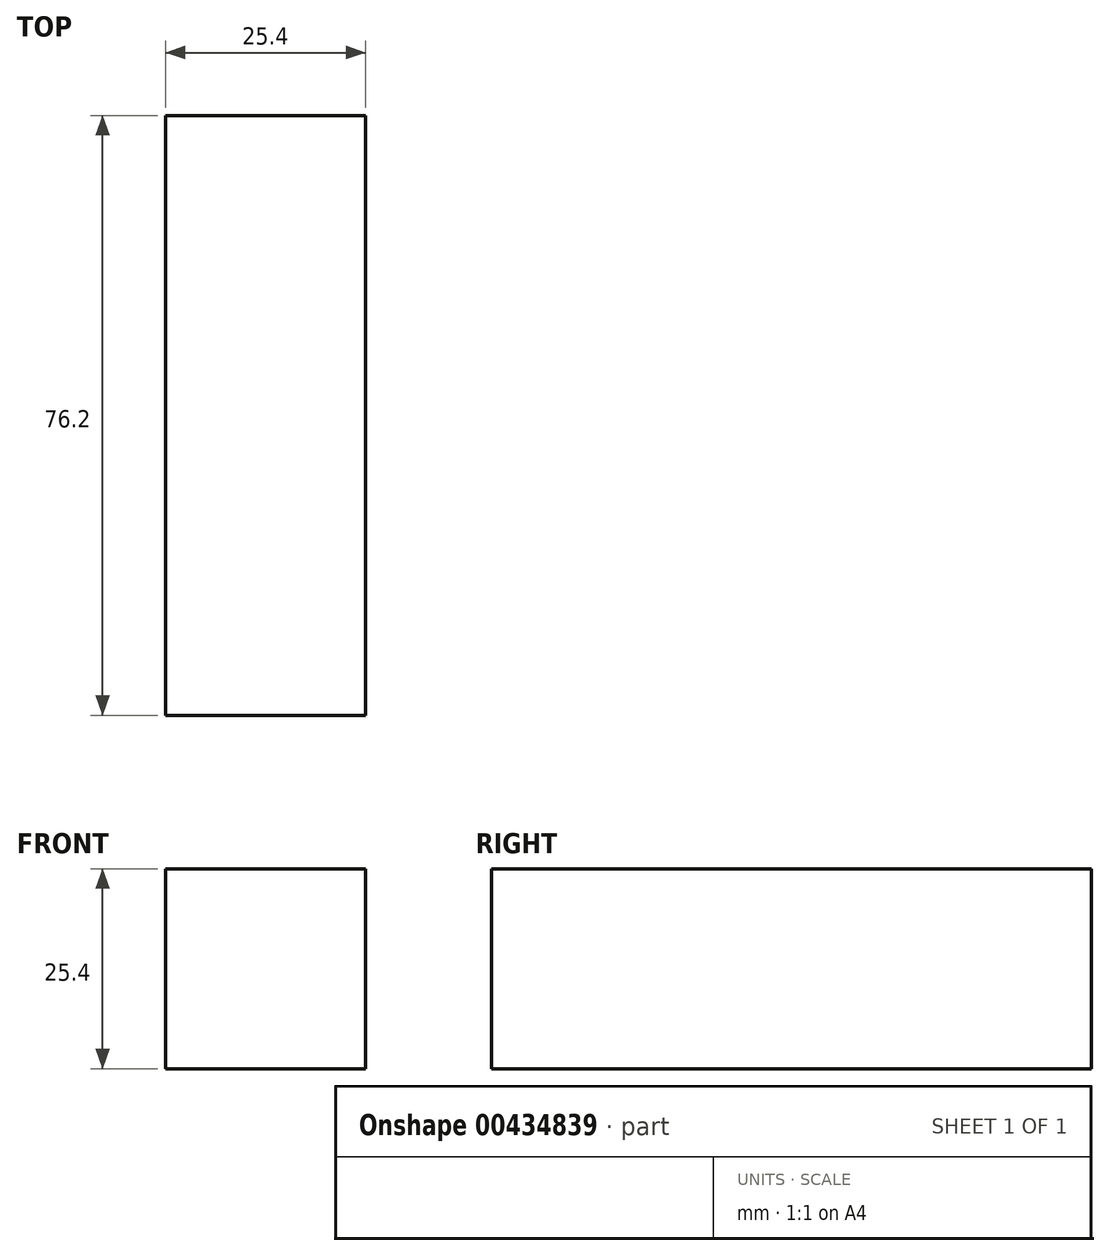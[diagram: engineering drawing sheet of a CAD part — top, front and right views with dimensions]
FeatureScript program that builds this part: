
annotation { "Feature Type Name" : "Feature", "Feature Type Description" : "" }
export const myFeature = defineFeature(function(context is Context, id is Id, definition is map)
    precondition{}
    {
        {
            var Q0;
            Q0=qCreatedBy(makeId("Front.planeOp"),FACE);
            var sketch = newSketch(context, id + "F0", { "sketchPlane" : qUnion([Q0])});
            skLineSegment(sketch, "E0.bottom", {"start": v(-13.75, 14.7) * mm, "end": v(11.65, 14.7) * mm});
            skLineSegment(sketch, "E0.top", {"start": v(-13.75, -10.7) * mm, "end": v(11.65, -10.7) * mm});
            skLineSegment(sketch, "E0.left", {"start": v(-13.75, 14.7) * mm, "end": v(-13.75, -10.7) * mm});
            skLineSegment(sketch, "E0.right", {"start": v(11.65, 14.7) * mm, "end": v(11.65, -10.7) * mm});
            skSolve(sketch);
        }
        {
            var Q0;
            Q0 = qSketchRegion(id + "F0", true);
            extrude(context, id + "F1", {"entities" : qUnion([Q0]), "depth" : 76.2 * mm});
        }
    });
